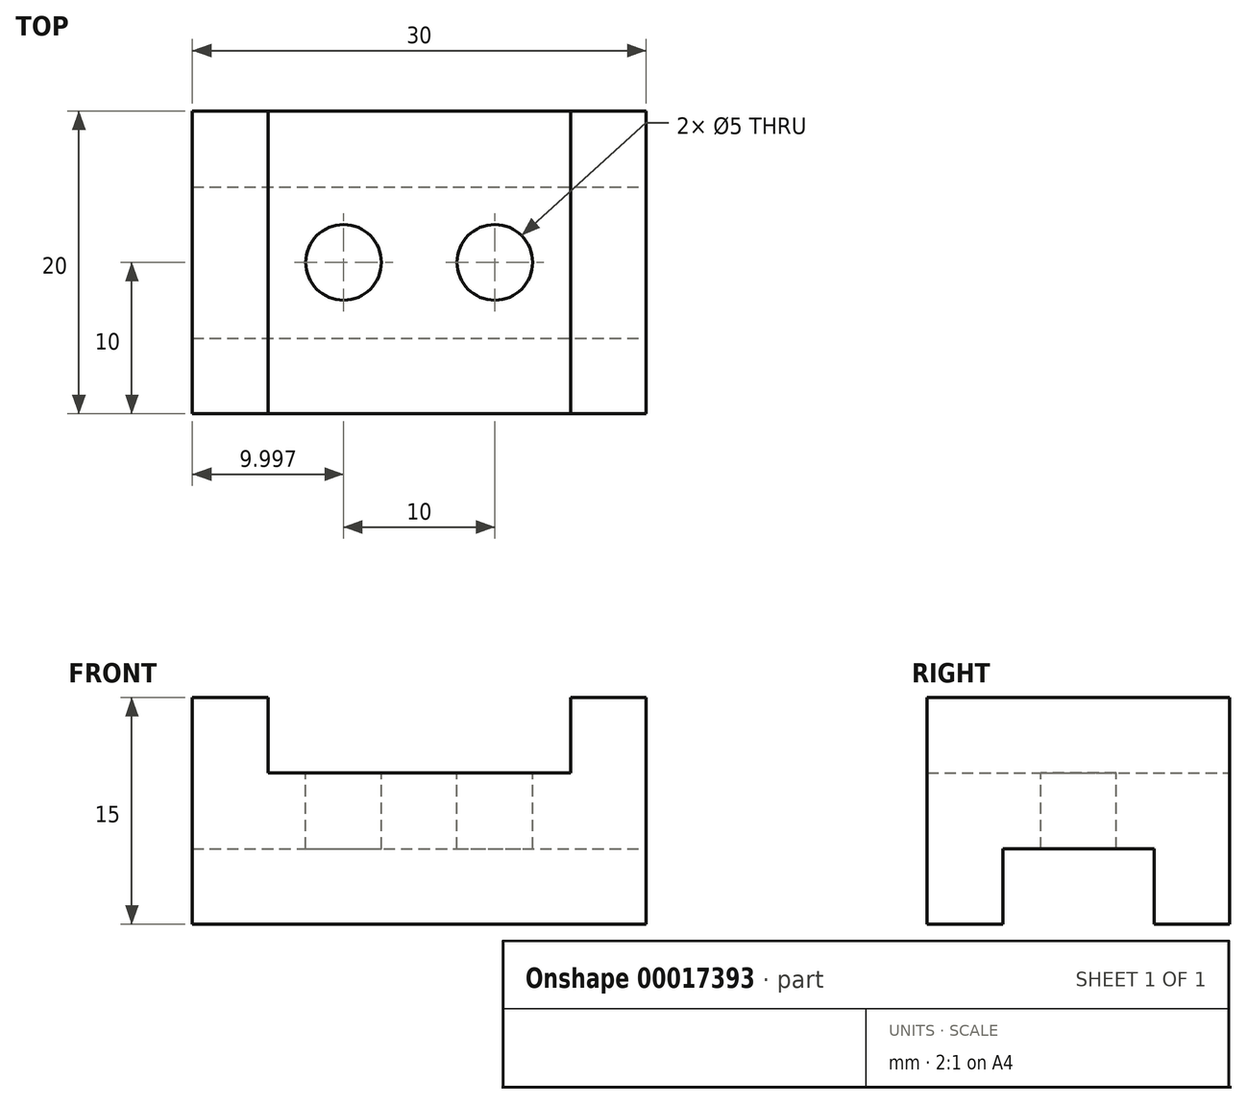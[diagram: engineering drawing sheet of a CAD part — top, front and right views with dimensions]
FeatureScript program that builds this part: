
annotation { "Feature Type Name" : "Feature", "Feature Type Description" : "" }
export const myFeature = defineFeature(function(context is Context, id is Id, definition is map)
    precondition{}
    {
        {
            var Q0;
            Q0=qCreatedBy(makeId("Front.planeOp"),FACE);
            var sketch = newSketch(context, id + "F0", { "sketchPlane" : qUnion([Q0])});
            skLineSegment(sketch, "E0", {"start": v(-17.48, 13.58) * mm, "end": v(-17.48, -1.42) * mm});
            skLineSegment(sketch, "E1", {"start": v(-17.48, -1.42) * mm, "end": v(12.52, -1.42) * mm});
            skLineSegment(sketch, "E2", {"start": v(12.52, -1.42) * mm, "end": v(12.52, 13.58) * mm});
            skLineSegment(sketch, "E3", {"start": v(12.52, 13.58) * mm, "end": v(7.52, 13.58) * mm});
            skLineSegment(sketch, "E4", {"start": v(7.52, 13.58) * mm, "end": v(7.52, 8.58) * mm});
            skLineSegment(sketch, "E5", {"start": v(7.52, 8.58) * mm, "end": v(-12.48, 8.58) * mm});
            skLineSegment(sketch, "E6", {"start": v(-12.48, 8.58) * mm, "end": v(-12.48, 13.58) * mm});
            skLineSegment(sketch, "E7", {"start": v(-12.48, 13.58) * mm, "end": v(-17.48, 13.58) * mm});
            skSolve(sketch);
        }
        {
            var Q0;
            Q0=makeQuery(id+"F0.imprint","IMPRINT",FACE,{"disambiguationData":[TD([[makeQuery(id+"F0.imprint","IMPRINT",EDGE,{"derivedFrom":sQuery(id+"F0.wireOp",EDGE,"E0")}),1.0]])]});
            extrude(context, id + "F1", {"entities" : qUnion([Q0]), "depth" : 20 * mm});
        }
        {
            var Q0;
            Q0=makeQuery(id+"F1.opExtrude","SWEPT_FACE",FACE,{"disambiguationData":[OSD([sQuery(id+"F0.wireOp",EDGE,"E2")])]});
            var sketch = newSketch(context, id + "F2", { "sketchPlane" : qUnion([Q0])});
            skLineSegment(sketch, "E8", {"start": v(-15, -1.42) * mm, "end": v(-15, 3.58) * mm});
            skLineSegment(sketch, "E9", {"start": v(-15, 3.58) * mm, "end": v(-5, 3.58) * mm});
            skLineSegment(sketch, "E10", {"start": v(-5, 3.58) * mm, "end": v(-5, -1.42) * mm});
            skSolve(sketch);
        }
        {
            var Q0;
            {var subQ2=sQuery(id+"F2.wireOp",EDGE,"E8");Q0=makeQuery(id+"F2.imprint","IMPRINT",FACE,{"disambiguationData":[TD([[makeQuery(id+"F2.imprint","IMPRINT",EDGE,{"derivedFrom":subQ2}),-1.0]])]});}
            extrude(context, id + "F3", {"entities" : qUnion([Q0]), "operationType" : NewBodyOperationType.REMOVE, "endBound" : BoundingType.THROUGH_ALL, "oppositeDirection" : true, "depth" : 25 * mm});
        }
        {
            var Q0;
            Q0=makeQuery(id+"F1.opExtrude","SWEPT_FACE",FACE,{"disambiguationData":[OSD([sQuery(id+"F0.wireOp",EDGE,"E5")])]});
            var sketch = newSketch(context, id + "F4", { "sketchPlane" : qUnion([Q0])});
            skCircle(sketch, "E11", {"center": v(-7.48, -10) * mm, "radius": 2.5 * mm});
            skCircle(sketch, "E12", {"center": v(2.52, -10) * mm, "radius": 2.5 * mm});
            skSolve(sketch);
        }
        {
            var Q0;
            {var subQ0=sQuery(id+"F0.wireOp",EDGE,"E5");Q0=makeQuery(id+"F4.imprint","IMPRINT",FACE,{"disambiguationData":[TD([[makeQuery(id+"F4.imprint","IMPRINT",EDGE,{"derivedFrom":makeQuery(id+"F1.opExtrude","CAP_EDGE",EDGE,{"disambiguationData":[OSD([subQ0])],"isStart":true})}),1.0]])]});}
            var sketch = newSketch(context, id + "F5", { "sketchPlane" : qUnion([Q0])});
            skSolve(sketch);
        }
        {
            var Q0;
            Q0=makeQuery(id+"F5.imprint","IMPRINT",FACE,{"disambiguationData":[TD([[makeQuery(id+"F5.imprint","IMPRINT",EDGE,{"derivedFrom":makeQuery(id+"F4.imprint","IMPRINT",EDGE,{"derivedFrom":sQuery(id+"F4.wireOp",EDGE,"E11")})}),1.0]])]});
            extrude(context, id + "F6", {"entities" : qUnion([Q0]), "operationType" : NewBodyOperationType.REMOVE, "endBound" : BoundingType.THROUGH_ALL, "oppositeDirection" : true, "depth" : 25 * mm});
        }
        {
            var Q0;
            Q0=makeQuery(id+"F4.imprint","IMPRINT",FACE,{"disambiguationData":[TD([[makeQuery(id+"F4.imprint","IMPRINT",EDGE,{"derivedFrom":sQuery(id+"F4.wireOp",EDGE,"E12")}),1.0]])]});
            var Q1;
            Q1=sQuery(id+"F4.wireOp",EDGE,"E12");
            extrude(context, id + "F7", {"entities" : qUnion([Q0]), "operationType" : NewBodyOperationType.REMOVE, "surfaceEntities" : qUnion([Q1]), "endBound" : BoundingType.THROUGH_ALL, "oppositeDirection" : true, "depth" : 25 * mm});
        }
    });
